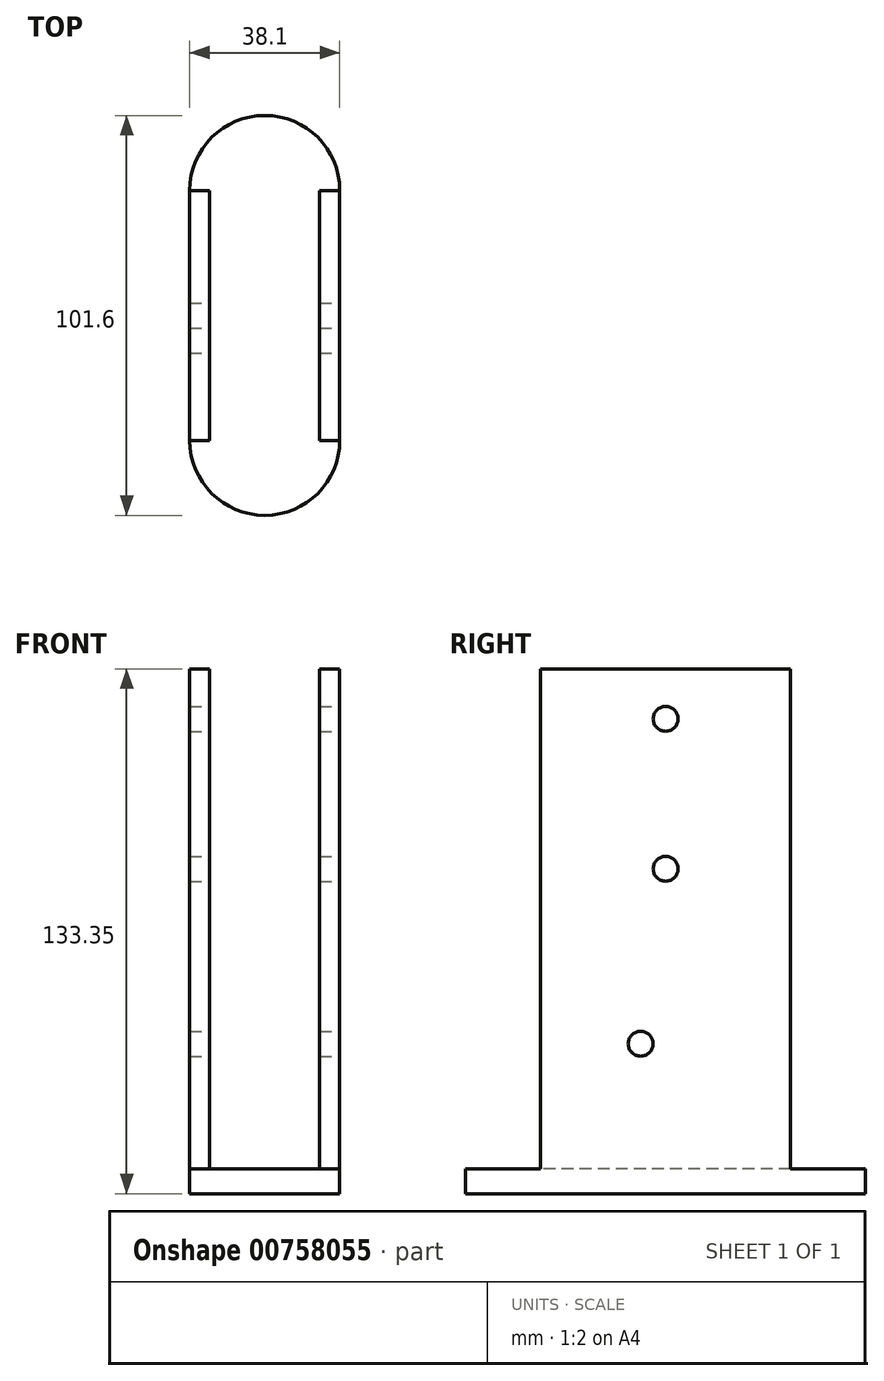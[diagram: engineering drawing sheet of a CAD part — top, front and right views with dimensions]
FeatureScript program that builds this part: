
annotation { "Feature Type Name" : "Feature", "Feature Type Description" : "" }
export const myFeature = defineFeature(function(context is Context, id is Id, definition is map)
    precondition{}
    {
        {
            var Q0;
            Q0=qCreatedBy(makeId("Top.planeOp"),FACE);
            var sketch = newSketch(context, id + "F0", { "sketchPlane" : qUnion([Q0])});
            skLineSegment(sketch, "E0.left", {"start": v(0, 0) * mm, "end": v(0, -63.5) * mm});
            skLineSegment(sketch, "E0.right", {"start": v(38.1, 0) * mm, "end": v(38.1, -63.5) * mm});
            skCircle(sketch, "E1", {"center": v(19.05, 0) * mm, "radius": 19.05 * mm, "construction": true});
            skCircle(sketch, "E2", {"center": v(19.05, -63.5) * mm, "radius": 19.05 * mm, "construction": true});
            skCircle(sketch, "E3", {"center": v(19.05, 0) * mm, "radius": 19.05 * mm});
            skCircle(sketch, "E4", {"center": v(19.05, -63.5) * mm, "radius": 19.05 * mm});
            skPoint(sketch, "E5", {"position": v(38.1, 0) * mm});
            skPoint(sketch, "E6", {"position": v(38.1, -63.5) * mm});
            skPoint(sketch, "E7", {"position": v(0, -63.5) * mm});
            skPoint(sketch, "E8", {"position": v(0, 0) * mm});
            skSolve(sketch);
        }
        {
            var Q0;
            {var subQ0=sQuery(id+"F0.wireOp",EDGE,"E0.left");Q0=makeQuery(id+"F0.imprint","IMPRINT",FACE,{"disambiguationData":[TD([[makeQuery(id+"F0.imprint","IMPRINT",EDGE,{"derivedFrom":subQ0}),1.0]])]});}
            var Q1;
            {var subQ0=sQuery(id+"F0.wireOp",EDGE,"E3");var subQ1=makeQuery(id+"F0.imprint","INTERSECT",VERTEX,{"derivedFrom":[sQuery(id+"F0.wireOp",EDGE,"E0.left"),subQ0]});Q1=makeQuery(id+"F0.imprint","IMPRINT",FACE,{"disambiguationData":[TD([[makeQuery(id+"F0.imprint","IMPRINT",EDGE,{"disambiguationData":[TD([[subQ1,1.0]])],"derivedFrom":subQ0}),1.0]])]});}
            var Q2;
            {var subQ0=sQuery(id+"F0.wireOp",EDGE,"E4");var subQ1=makeQuery(id+"F0.imprint","INTERSECT",VERTEX,{"derivedFrom":[sQuery(id+"F0.wireOp",EDGE,"E0.left"),subQ0]});Q2=makeQuery(id+"F0.imprint","IMPRINT",FACE,{"disambiguationData":[TD([[makeQuery(id+"F0.imprint","IMPRINT",EDGE,{"disambiguationData":[TD([[subQ1,1.0]])],"derivedFrom":subQ0}),1.0]])]});}
            extrude(context, id + "F1", {"entities" : qUnion([Q0, Q1, Q2]), "depth" : 6.35 * mm, "offsetDistance" : 25.4 * mm});
        }
        {
            var Q0;
            Q0=makeQuery(id+"F1.opExtrude","CAP_FACE",FACE,{"disambiguationData":[OSD([sQuery(id+"F0.wireOp",EDGE,"E0.left"),sQuery(id+"F0.wireOp",EDGE,"E0.right"),sQuery(id+"F0.wireOp",EDGE,"E3"),sQuery(id+"F0.wireOp",EDGE,"E4")])],"isStart":false});
            var sketch = newSketch(context, id + "F2", { "sketchPlane" : qUnion([Q0])});
            skPoint(sketch, "E9", {"position": v(38.1, 0) * mm});
            skPoint(sketch, "E10", {"position": v(38.1, -63.5) * mm});
            skPoint(sketch, "E11", {"position": v(0, -63.5) * mm});
            skLineSegment(sketch, "E12.bottom", {"start": v(0, 0) * mm, "end": v(5.08, 0) * mm});
            skLineSegment(sketch, "E12.top", {"start": v(0, -63.5) * mm, "end": v(5.08, -63.5) * mm});
            skLineSegment(sketch, "E12.left", {"start": v(0, 0) * mm, "end": v(0, -63.5) * mm});
            skLineSegment(sketch, "E12.right", {"start": v(5.08, 0) * mm, "end": v(5.08, -63.5) * mm});
            skLineSegment(sketch, "E13.bottom", {"start": v(38.1, 0) * mm, "end": v(33.02, 0) * mm});
            skLineSegment(sketch, "E13.top", {"start": v(38.1, -63.5) * mm, "end": v(33.02, -63.5) * mm});
            skLineSegment(sketch, "E13.left", {"start": v(38.1, 0) * mm, "end": v(38.1, -63.5) * mm});
            skLineSegment(sketch, "E13.right", {"start": v(33.02, 0) * mm, "end": v(33.02, -63.5) * mm});
            skSolve(sketch);
        }
        {
            var Q0;
            Q0=makeQuery(id+"F2.imprint","IMPRINT",FACE,{"disambiguationData":[TD([[makeQuery(id+"F2.imprint","IMPRINT",EDGE,{"derivedFrom":sQuery(id+"F2.wireOp",EDGE,"E12.bottom")}),-1.0]])]});
            var Q1;
            Q1=makeQuery(id+"F2.imprint","IMPRINT",FACE,{"disambiguationData":[TD([[makeQuery(id+"F2.imprint","IMPRINT",EDGE,{"derivedFrom":sQuery(id+"F2.wireOp",EDGE,"E13.bottom")}),1.0]])]});
            extrude(context, id + "F3", {"entities" : qUnion([Q0, Q1]), "operationType" : NewBodyOperationType.ADD, "depth" : 127 * mm, "offsetDistance" : 25.4 * mm});
        }
        {
            var Q0;
            Q0=makeQuery(id+"F3.boolean.opBoolean","MERGE",FACE,{"derivedFrom":[makeQuery(id+"F1.opExtrude","SWEPT_FACE",FACE,{"disambiguationData":[OSD([sQuery(id+"F0.wireOp",EDGE,"E0.right")])]}),makeQuery(id+"F3.opExtrude","SWEPT_FACE",FACE,{"disambiguationData":[OSD([sQuery(id+"F2.wireOp",EDGE,"E13.left")])]})]});
            var sketch = newSketch(context, id + "F4", { "sketchPlane" : qUnion([Q0])});
            skCircle(sketch, "E14", {"center": v(-31.75, 120.65) * mm, "radius": 3.18 * mm});
            skCircle(sketch, "E15", {"center": v(-31.75, 82.55) * mm, "radius": 3.18 * mm});
            skCircle(sketch, "E16", {"center": v(-38.1, 38.1) * mm, "radius": 3.18 * mm});
            skSolve(sketch);
        }
        {
            var Q0;
            Q0=makeQuery(id+"F4.imprint","IMPRINT",FACE,{"disambiguationData":[TD([[makeQuery(id+"F4.imprint","IMPRINT",EDGE,{"derivedFrom":sQuery(id+"F4.wireOp",EDGE,"E14")}),1.0]])]});
            var Q1;
            Q1=makeQuery(id+"F4.imprint","IMPRINT",FACE,{"disambiguationData":[TD([[makeQuery(id+"F4.imprint","IMPRINT",EDGE,{"derivedFrom":sQuery(id+"F4.wireOp",EDGE,"E15")}),1.0]])]});
            var Q2;
            Q2=makeQuery(id+"F4.imprint","IMPRINT",FACE,{"disambiguationData":[TD([[makeQuery(id+"F4.imprint","IMPRINT",EDGE,{"derivedFrom":sQuery(id+"F4.wireOp",EDGE,"E16")}),1.0]])]});
            extrude(context, id + "F5", {"entities" : qUnion([Q0, Q1, Q2]), "operationType" : NewBodyOperationType.REMOVE, "oppositeDirection" : true, "depth" : 50.8 * mm, "offsetDistance" : 25.4 * mm});
        }
    });
